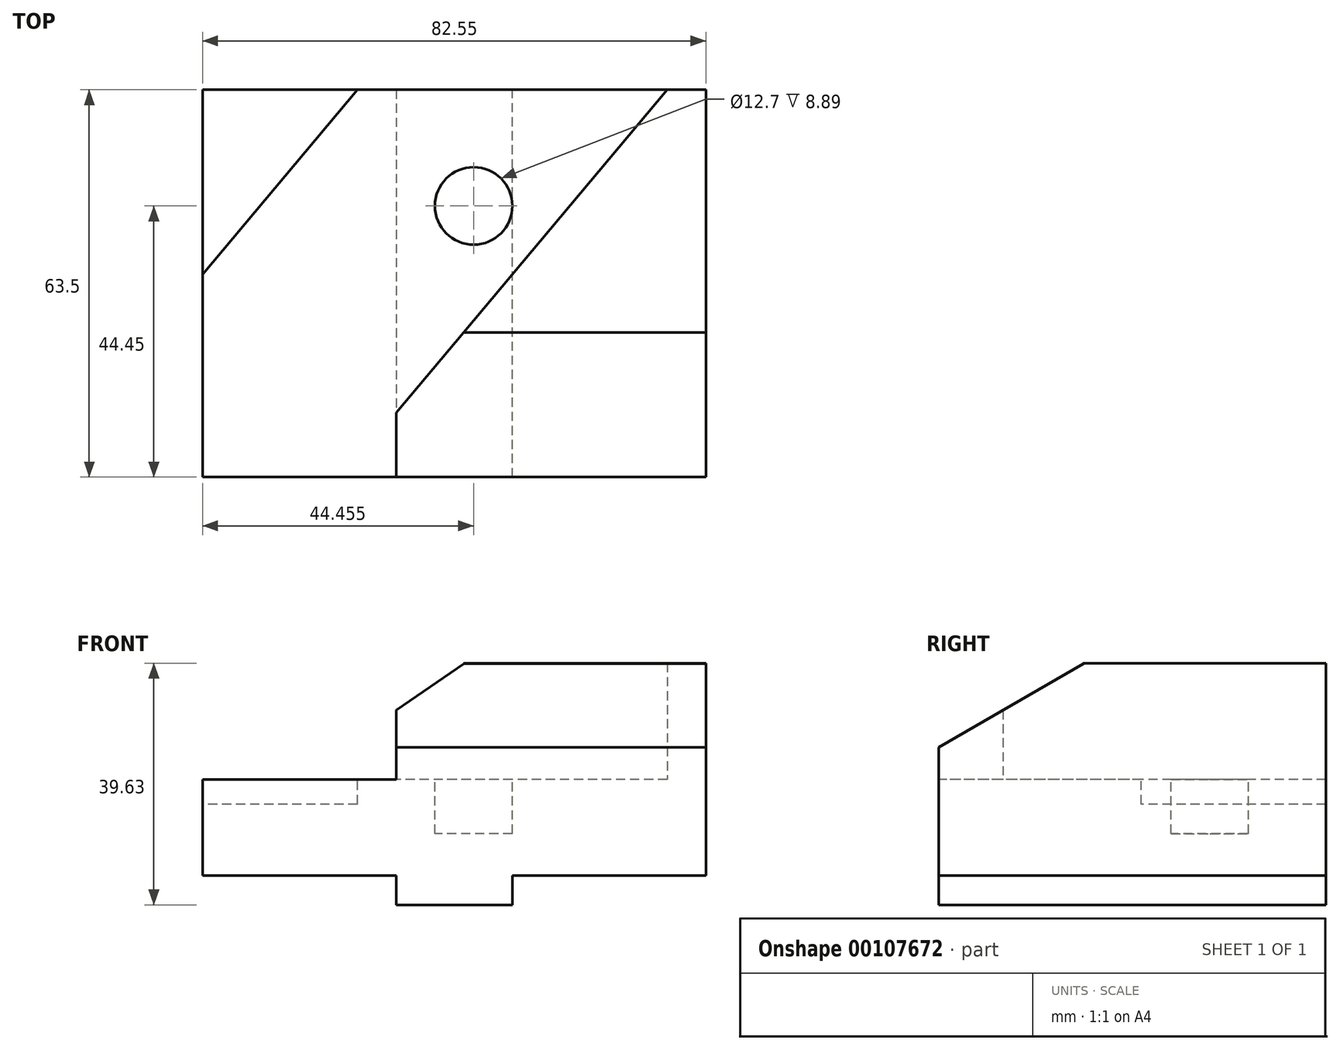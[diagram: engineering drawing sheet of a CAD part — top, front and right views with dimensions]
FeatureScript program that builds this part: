
annotation { "Feature Type Name" : "Feature", "Feature Type Description" : "" }
export const myFeature = defineFeature(function(context is Context, id is Id, definition is map)
    precondition{}
    {
        {
            var Q0;
            Q0=qCreatedBy(makeId("Top.planeOp"),FACE);
            var sketch = newSketch(context, id + "F0", { "sketchPlane" : qUnion([Q0])});
            skLineSegment(sketch, "E0.bottom", {"start": v(41.28, 31.75) * mm, "end": v(-41.27, 31.75) * mm});
            skLineSegment(sketch, "E0.top", {"start": v(41.27, -31.75) * mm, "end": v(-41.28, -31.75) * mm});
            skLineSegment(sketch, "E0.left", {"start": v(41.28, 31.75) * mm, "end": v(41.27, -31.75) * mm});
            skLineSegment(sketch, "E0.right", {"start": v(-41.27, 31.75) * mm, "end": v(-41.28, -31.75) * mm});
            skPoint(sketch, "E0.middle", {"position": v(0, 0) * mm});
            skSolve(sketch);
        }
        {
            var Q0;
            Q0 = qSketchRegion(id + "F0", true);
            extrude(context, id + "F1", {"entities" : qUnion([Q0]), "depth" : 15.75 * mm});
        }
        {
            var Q0;
            Q0=makeQuery(id+"F1.opExtrude","CAP_FACE",FACE,{"disambiguationData":[OSD([sQuery(id+"F0.wireOp",EDGE,"E0.bottom"),sQuery(id+"F0.wireOp",EDGE,"E0.top"),sQuery(id+"F0.wireOp",EDGE,"E0.left"),sQuery(id+"F0.wireOp",EDGE,"E0.right")])],"isStart":false});
            var sketch = newSketch(context, id + "F2", { "sketchPlane" : qUnion([Q0])});
            skLineSegment(sketch, "E1", {"start": v(-15.87, 31.75) * mm, "end": v(-41.28, 1.48) * mm});
            skLineSegment(sketch, "E2", {"start": v(-41.28, 1.48) * mm, "end": v(-41.27, 31.75) * mm});
            skLineSegment(sketch, "E3", {"start": v(-41.27, 31.75) * mm, "end": v(-15.87, 31.75) * mm});
            skSolve(sketch);
        }
        {
            var Q0;
            Q0 = qSketchRegion(id + "F2", true);
            extrude(context, id + "F3", {"entities" : qUnion([Q0]), "operationType" : NewBodyOperationType.REMOVE, "oppositeDirection" : true, "depth" : 4.06 * mm});
        }
        {
            var Q0;
            Q0=makeQuery(id+"F1.opExtrude","CAP_FACE",FACE,{"disambiguationData":[OSD([sQuery(id+"F0.wireOp",EDGE,"E0.bottom"),sQuery(id+"F0.wireOp",EDGE,"E0.top"),sQuery(id+"F0.wireOp",EDGE,"E0.left"),sQuery(id+"F0.wireOp",EDGE,"E0.right")])],"isStart":true});
            var sketch = newSketch(context, id + "F4", { "sketchPlane" : qUnion([Q0])});
            skLineSegment(sketch, "E4", {"start": v(9.53, 31.75) * mm, "end": v(9.53, -31.75) * mm});
            skLineSegment(sketch, "E5", {"start": v(9.53, -31.75) * mm, "end": v(-9.53, -31.75) * mm});
            skLineSegment(sketch, "E6", {"start": v(-9.52, -31.75) * mm, "end": v(-9.52, 31.75) * mm});
            skLineSegment(sketch, "E7", {"start": v(-9.53, 31.75) * mm, "end": v(9.52, 31.75) * mm});
            skSolve(sketch);
        }
        {
            var Q0;
            Q0 = qSketchRegion(id + "F4", true);
            extrude(context, id + "F5", {"entities" : qUnion([Q0]), "operationType" : NewBodyOperationType.ADD, "depth" : 4.83 * mm});
        }
        {
            var Q0;
            Q0=makeQuery(id+"F1.opExtrude","CAP_FACE",FACE,{"disambiguationData":[OSD([sQuery(id+"F0.wireOp",EDGE,"E0.bottom"),sQuery(id+"F0.wireOp",EDGE,"E0.top"),sQuery(id+"F0.wireOp",EDGE,"E0.left"),sQuery(id+"F0.wireOp",EDGE,"E0.right")])],"isStart":false});
            var sketch = newSketch(context, id + "F6", { "sketchPlane" : qUnion([Q0])});
            skLineSegment(sketch, "E8", {"start": v(41.28, 31.75) * mm, "end": v(34.93, 31.75) * mm});
            skLineSegment(sketch, "E9", {"start": v(34.93, 31.75) * mm, "end": v(-18.36, -31.75) * mm});
            skLineSegment(sketch, "E10", {"start": v(-18.36, -31.75) * mm, "end": v(41.27, -31.75) * mm});
            skLineSegment(sketch, "E11", {"start": v(41.27, -31.75) * mm, "end": v(41.28, 31.75) * mm});
            skSolve(sketch);
        }
        {
            var Q0;
            Q0=makeQuery(id+"F6.imprint","IMPRINT",FACE,{"disambiguationData":[TD([[makeQuery(id+"F6.imprint","IMPRINT",EDGE,{"derivedFrom":sQuery(id+"F6.wireOp",EDGE,"E8")}),1.0]])]});
            extrude(context, id + "F7", {"entities" : qUnion([Q0]), "operationType" : NewBodyOperationType.ADD, "depth" : 19.05 * mm});
        }
        {
            var Q0;
            Q0=makeQuery(id+"F1.opExtrude","CAP_FACE",FACE,{"disambiguationData":[OSD([sQuery(id+"F0.wireOp",EDGE,"E0.bottom"),sQuery(id+"F0.wireOp",EDGE,"E0.top"),sQuery(id+"F0.wireOp",EDGE,"E0.left"),sQuery(id+"F0.wireOp",EDGE,"E0.right")])],"isStart":false});
            var sketch = newSketch(context, id + "F8", { "sketchPlane" : qUnion([Q0])});
            skCircle(sketch, "E12", {"center": v(3.18, 12.7) * mm, "radius": 6.35 * mm});
            skSolve(sketch);
        }
        {
            var Q0;
            Q0 = qSketchRegion(id + "F8", true);
            extrude(context, id + "F9", {"entities" : qUnion([Q0]), "operationType" : NewBodyOperationType.REMOVE, "oppositeDirection" : true, "depth" : 8.9 * mm});
        }
        {
            var Q0;
            Q0=makeQuery(id+"F7.opExtrude","CAP_FACE",FACE,{"disambiguationData":[OSD([sQuery(id+"F6.wireOp",EDGE,"E8"),sQuery(id+"F6.wireOp",EDGE,"E9"),sQuery(id+"F6.wireOp",EDGE,"E10"),sQuery(id+"F6.wireOp",EDGE,"E11")])],"isStart":false});
            var sketch = newSketch(context, id + "F10", { "sketchPlane" : qUnion([Q0])});
            skLineSegment(sketch, "E13", {"start": v(41.28, -7.87) * mm, "end": v(1.68, -7.87) * mm});
            skSolve(sketch);
        }
        {
            var Q0;
            Q0=makeQuery(id+"F7.boolean.opBoolean","MERGE",FACE,{"derivedFrom":[makeQuery(id+"F5.boolean.opBoolean","MERGE",FACE,{"derivedFrom":[makeQuery(id+"F1.opExtrude","SWEPT_FACE",FACE,{"disambiguationData":[OSD([sQuery(id+"F0.wireOp",EDGE,"E0.top")])]}),makeQuery(id+"F5.opExtrude","SWEPT_FACE",FACE,{"disambiguationData":[OSD([sQuery(id+"F4.wireOp",EDGE,"E7")])]})]}),makeQuery(id+"F7.opExtrude","SWEPT_FACE",FACE,{"disambiguationData":[OSD([sQuery(id+"F6.wireOp",EDGE,"E10")])]})]});
            var sketch = newSketch(context, id + "F11", { "sketchPlane" : qUnion([Q0])});
            skLineSegment(sketch, "E14", {"start": v(41.27, 21.01) * mm, "end": v(-18.36, 21.01) * mm});
            skSolve(sketch);
        }
        {
            var Q0;
            Q0=sQuery(id+"F11.wireOp",EDGE,"E14");
            var Q1;
            Q1=sQuery(id+"F10.wireOp",EDGE,"E13");
            cPlane(context, id + "F12", {"entities" : qUnion([Q0, Q1]), "cplaneType" : CPlaneType.LINE_ANGLE, "offset" : 25.4 * mm, "angle" : 0 * degree, "width" : 152.4 * mm, "height" : 152.4 * mm});
        }
        {
            var Q0;
            Q0=qCreatedBy(id+"F12.planeOp",FACE);
            var sketch = newSketch(context, id + "F13", { "sketchPlane" : qUnion([Q0])});
            skLineSegment(sketch, "E15", {"start": v(-20.11, 17.11) * mm, "end": v(0, -10.44) * mm});
            skLineSegment(sketch, "E16", {"start": v(0, -10.44) * mm, "end": v(43.62, -10.44) * mm});
            skLineSegment(sketch, "E17", {"start": v(43.62, -10.44) * mm, "end": v(43.62, 20.47) * mm});
            skLineSegment(sketch, "E18", {"start": v(43.62, 20.47) * mm, "end": v(-18.58, 20.47) * mm});
            skLineSegment(sketch, "E19", {"start": v(-18.58, 20.47) * mm, "end": v(-20.11, 17.11) * mm});
            skSolve(sketch);
        }
        {
            var Q0;
            Q0 = qSketchRegion(id + "F13", true);
            extrude(context, id + "F14", {"entities" : qUnion([Q0]), "operationType" : NewBodyOperationType.REMOVE, "oppositeDirection" : true, "depth" : 25.4 * mm});
        }
        {
            var Q0;
            {var subQ1=sQuery(id+"F6.wireOp",EDGE,"E9");Q0=makeQuery(id+"F14.boolean.opBoolean","SPLIT",FACE,{"disambiguationData":[TD([makeQuery(id+"F14.opExtrude","SWEPT_FACE",FACE,{"disambiguationData":[OSD([sQuery(id+"F13.wireOp",EDGE,"E15")])]})])],"derivedFrom":makeQuery(id+"F7.opExtrude","SWEPT_FACE",FACE,{"disambiguationData":[OSD([subQ1])]})});}
            var sketch = newSketch(context, id + "F15", { "sketchPlane" : qUnion([Q0])});
            skLineSegment(sketch, "E20", {"start": v(14.89, 34.8) * mm, "end": v(36.12, 25.57) * mm});
            skLineSegment(sketch, "E21", {"start": v(36.12, 25.57) * mm, "end": v(36.12, 34.8) * mm});
            skLineSegment(sketch, "E22", {"start": v(36.12, 34.8) * mm, "end": v(14.89, 34.8) * mm});
            skSolve(sketch);
        }
        {
            var Q0;
            Q0 = qSketchRegion(id + "F15", true);
            extrude(context, id + "F16", {"entities" : qUnion([Q0]), "operationType" : NewBodyOperationType.REMOVE, "oppositeDirection" : true, "depth" : 25.4 * mm});
        }
        {
            var Q0;
            Q0=makeQuery(id+"F1.opExtrude","SWEPT_FACE",FACE,{"disambiguationData":[OSD([sQuery(id+"F0.wireOp",EDGE,"E0.right")])]});
            cPlane(context, id + "F17", {"entities" : qUnion([Q0]), "cplaneType" : CPlaneType.OFFSET, "offset" : 0 * mm, "width" : 152.4 * mm, "height" : 152.4 * mm});
        }
        {
            var Q0;
            Q0=qCreatedBy(id+"F17.planeOp",FACE);
            var sketch = newSketch(context, id + "F18", { "sketchPlane" : qUnion([Q0])});
            skLineSegment(sketch, "E23.bottom", {"start": v(15.54, 15.75) * mm, "end": v(39.47, 15.75) * mm});
            skLineSegment(sketch, "E23.top", {"start": v(15.54, 33.4) * mm, "end": v(39.47, 33.4) * mm});
            skLineSegment(sketch, "E23.left", {"start": v(15.54, 15.75) * mm, "end": v(15.54, 33.4) * mm});
            skLineSegment(sketch, "E23.right", {"start": v(39.47, 15.75) * mm, "end": v(39.47, 33.4) * mm});
            skSolve(sketch);
        }
        {
            var Q0;
            Q0=makeQuery(id+"F18.imprint","IMPRINT",FACE,{"disambiguationData":[TD([[makeQuery(id+"F18.imprint","IMPRINT",EDGE,{"derivedFrom":sQuery(id+"F18.wireOp",EDGE,"E23.bottom")}),1.0]])]});
            extrude(context, id + "F19", {"entities" : qUnion([Q0]), "operationType" : NewBodyOperationType.REMOVE, "oppositeDirection" : true, "depth" : 31.75 * mm});
        }
    });
